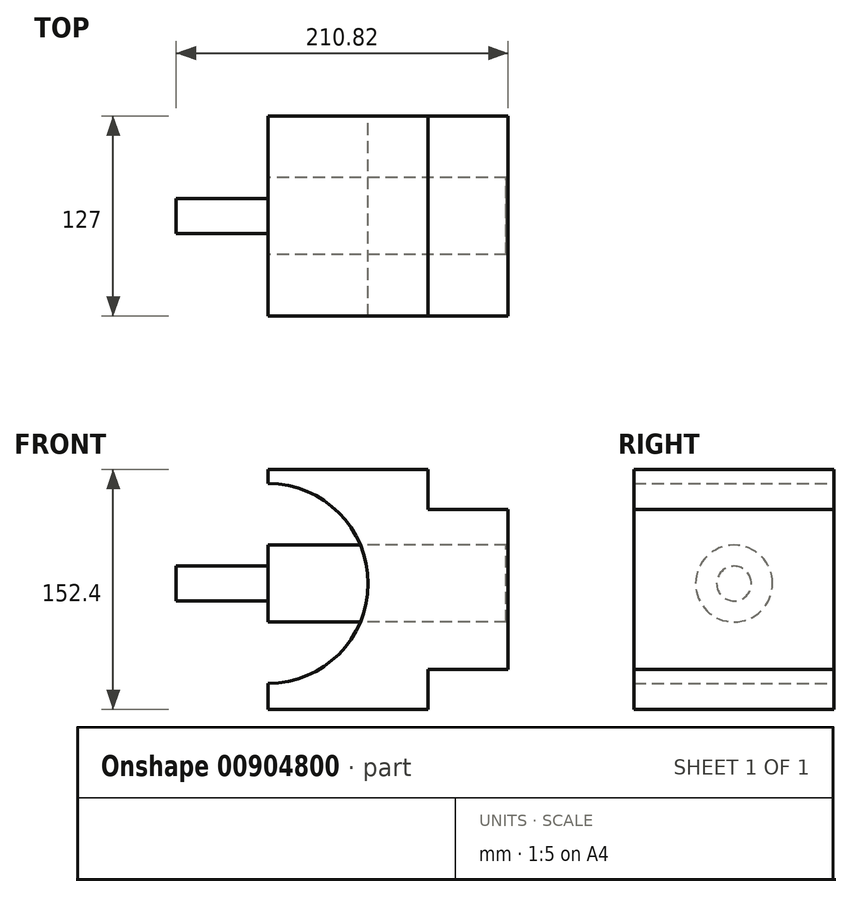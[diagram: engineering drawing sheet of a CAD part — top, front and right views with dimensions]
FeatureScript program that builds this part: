
annotation { "Feature Type Name" : "Feature", "Feature Type Description" : "" }
export const myFeature = defineFeature(function(context is Context, id is Id, definition is map)
    precondition{}
    {
        {
            var Q0;
            Q0=qCreatedBy(makeId("Front.planeOp"),FACE);
            var sketch = newSketch(context, id + "F0", { "sketchPlane" : qUnion([Q0])});
            skLineSegment(sketch, "E0", {"start": v(0, -79.97) * mm, "end": v(0, -63.5) * mm});
            skLineSegment(sketch, "E1", {"start": v(0, 72.43) * mm, "end": v(101.6, 72.43) * mm});
            skLineSegment(sketch, "E2", {"start": v(101.6, 72.43) * mm, "end": v(101.6, 47.03) * mm});
            skLineSegment(sketch, "E3", {"start": v(101.6, 47.03) * mm, "end": v(152.4, 47.03) * mm});
            skLineSegment(sketch, "E4", {"start": v(152.4, 47.03) * mm, "end": v(152.4, -54.57) * mm});
            skLineSegment(sketch, "E5", {"start": v(152.4, -54.57) * mm, "end": v(101.6, -54.57) * mm});
            skLineSegment(sketch, "E6", {"start": v(101.6, -54.57) * mm, "end": v(101.6, -79.97) * mm});
            skLineSegment(sketch, "E7", {"start": v(101.6, -79.97) * mm, "end": v(0, -79.97) * mm});
            skArc(sketch, "E8", {"start": v(0, -63.5) * mm, "mid": v(63.5, 0) * mm, "end": v(0, 63.5) * mm});
            skLineSegment(sketch, "E9.trimOffspring", {"start": v(0, 63.5) * mm, "end": v(0, 72.43) * mm});
            skSolve(sketch);
        }
        {
            var Q0;
            Q0=makeQuery(id+"F0.imprint","IMPRINT",FACE,{"disambiguationData":[TD([[makeQuery(id+"F0.imprint","IMPRINT",EDGE,{"derivedFrom":sQuery(id+"F0.wireOp",EDGE,"E0")}),-1.0]])]});
            extrude(context, id + "F1", {"entities" : qUnion([Q0]), "depth" : 127 * mm, "offsetDistance" : 25.4 * mm, "symmetric" : true});
        }
        {
            var Q0;
            Q0=qCreatedBy(makeId("Right.planeOp"),FACE);
            var sketch = newSketch(context, id + "F2", { "sketchPlane" : qUnion([Q0])});
            skCircle(sketch, "E10", {"center": v(0, 0) * mm, "radius": 24.41 * mm});
            skSolve(sketch);
        }
        {
            var Q0;
            Q0=makeQuery(id+"F2.imprint","IMPRINT",FACE,{"disambiguationData":[TD([[makeQuery(id+"F2.imprint","IMPRINT",EDGE,{"derivedFrom":sQuery(id+"F2.wireOp",EDGE,"E10")}),1.0]])]});
            extrude(context, id + "F3", {"entities" : qUnion([Q0]), "depth" : 151.13 * mm, "offsetDistance" : 25.4 * mm});
        }
        {
            var Q0;
            Q0=qCreatedBy(makeId("Right.planeOp"),FACE);
            var sketch = newSketch(context, id + "F4", { "sketchPlane" : qUnion([Q0])});
            skCircle(sketch, "E11", {"center": v(0, 0) * mm, "radius": 11.06 * mm});
            skSolve(sketch);
        }
        {
            var Q0;
            Q0=makeQuery(id+"F4.imprint","IMPRINT",FACE,{"disambiguationData":[TD([[makeQuery(id+"F4.imprint","IMPRINT",EDGE,{"derivedFrom":sQuery(id+"F4.wireOp",EDGE,"E11")}),1.0]])]});
            extrude(context, id + "F5", {"entities" : qUnion([Q0]), "operationType" : NewBodyOperationType.ADD, "oppositeDirection" : true, "depth" : 58.42 * mm, "offsetDistance" : 25.4 * mm});
        }
    });
